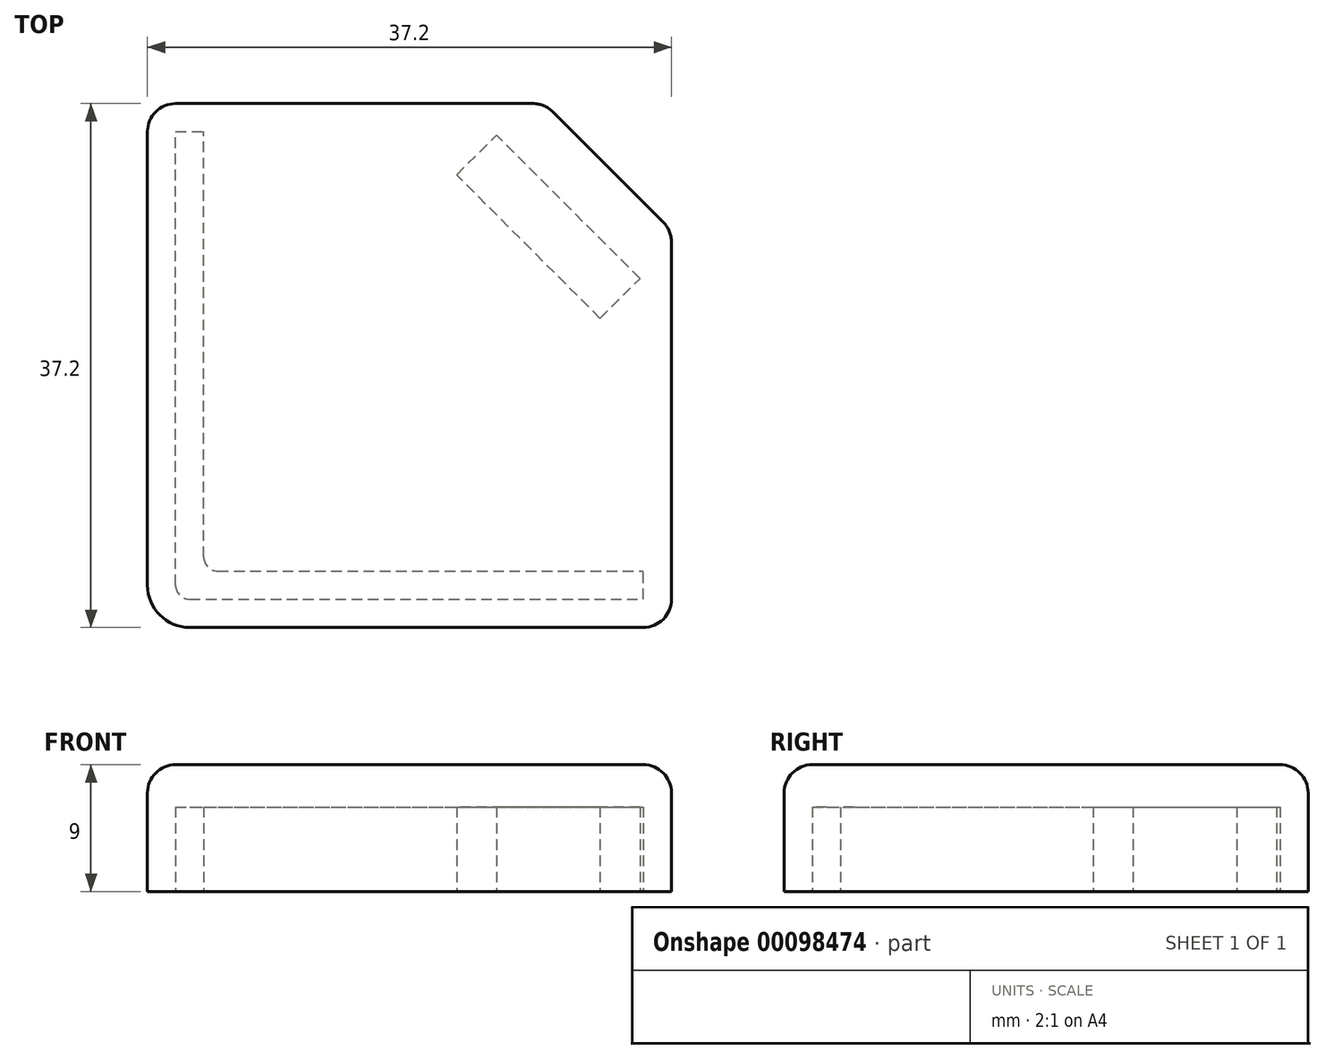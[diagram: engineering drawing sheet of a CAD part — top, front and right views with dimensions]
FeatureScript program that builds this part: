
annotation { "Feature Type Name" : "Feature", "Feature Type Description" : "" }
export const myFeature = defineFeature(function(context is Context, id is Id, definition is map)
    precondition{}
    {
        {
            var Q0;
            Q0=qCreatedBy(makeId("Top.planeOp"),FACE);
            var sketch = newSketch(context, id + "F0", { "sketchPlane" : qUnion([Q0])});
            skLineSegment(sketch, "E0", {"start": v(0, 0) * mm, "end": v(0, 32.2) * mm, "construction": true});
            skLineSegment(sketch, "E1", {"start": v(0, 0) * mm, "end": v(32.2, 0) * mm, "construction": true});
            skLineSegment(sketch, "E2.0", {"start": v(1, 2) * mm, "end": v(1, 32.2) * mm});
            skLineSegment(sketch, "E2.1", {"start": v(2, 1) * mm, "end": v(32.2, 1) * mm});
            skLineSegment(sketch, "E3.0", {"start": v(-1, 0) * mm, "end": v(-1, 32.2) * mm});
            skLineSegment(sketch, "E3.1", {"start": v(0, -1) * mm, "end": v(32.2, -1) * mm});
            skLineSegment(sketch, "E4", {"start": v(-1, 32.2) * mm, "end": v(1, 32.2) * mm});
            skLineSegment(sketch, "E5", {"start": v(32.2, -1) * mm, "end": v(32.2, 1) * mm});
            skPoint(sketch, "E6.visualSharp", {"position": v(1, 1) * mm});
            skArc(sketch, "E6.filletArc", {"start": v(1, 2) * mm, "mid": v(1.3, 1.3) * mm, "end": v(2, 1) * mm});
            skPoint(sketch, "E7.visualSharp", {"position": v(-1, -1) * mm});
            skArc(sketch, "E7.filletArc", {"start": v(-1, 0) * mm, "mid": v(-0.7, -0.7) * mm, "end": v(0, -1) * mm});
            skLineSegment(sketch, "E8.0", {"start": v(-3, 0) * mm, "end": v(-3, 34.2) * mm});
            skArc(sketch, "E8.1", {"start": v(-3, 0) * mm, "mid": v(-2.12, -2.12) * mm, "end": v(0, -3) * mm});
            skLineSegment(sketch, "E8.2", {"start": v(3, 5) * mm, "end": v(3, 34.2) * mm});
            skLineSegment(sketch, "E8.3", {"start": v(5, 3) * mm, "end": v(34.2, 3) * mm});
            skLineSegment(sketch, "E8.4", {"start": v(34.2, -3) * mm, "end": v(34.2, 3) * mm});
            skLineSegment(sketch, "E8.5", {"start": v(-3, 34.2) * mm, "end": v(3, 34.2) * mm});
            skLineSegment(sketch, "E8.6", {"start": v(0, -3) * mm, "end": v(34.2, -3) * mm});
            skPoint(sketch, "E9.visualSharp", {"position": v(3, 3) * mm});
            skArc(sketch, "E9.filletArc", {"start": v(3, 5) * mm, "mid": v(3.59, 3.59) * mm, "end": v(5, 3) * mm});
            skSolve(sketch);
        }
        {
            var Q0;
            Q0=makeQuery(id+"F0.imprint","IMPRINT",FACE,{"disambiguationData":[TD([[makeQuery(id+"F0.imprint","IMPRINT",EDGE,{"derivedFrom":sQuery(id+"F0.wireOp",EDGE,"E2.0")}),-1.0]])]});
            extrude(context, id + "F1", {"entities" : qUnion([Q0]), "depth" : 6 * mm});
        }
        {
            var Q0;
            Q0=makeQuery(id+"F1.opExtrude","CAP_FACE",FACE,{"disambiguationData":[OSD([sQuery(id+"F0.wireOp",EDGE,"E2.0"),sQuery(id+"F0.wireOp",EDGE,"E2.1"),sQuery(id+"F0.wireOp",EDGE,"E3.0"),sQuery(id+"F0.wireOp",EDGE,"E3.1"),sQuery(id+"F0.wireOp",EDGE,"E4"),sQuery(id+"F0.wireOp",EDGE,"E5"),sQuery(id+"F0.wireOp",EDGE,"E6.filletArc"),sQuery(id+"F0.wireOp",EDGE,"E7.filletArc"),sQuery(id+"F0.wireOp",EDGE,"E8.0"),sQuery(id+"F0.wireOp",EDGE,"E8.1"),sQuery(id+"F0.wireOp",EDGE,"E8.2"),sQuery(id+"F0.wireOp",EDGE,"E8.3"),sQuery(id+"F0.wireOp",EDGE,"E8.4"),sQuery(id+"F0.wireOp",EDGE,"E8.5"),sQuery(id+"F0.wireOp",EDGE,"E8.6"),sQuery(id+"F0.wireOp",EDGE,"E9.filletArc")])],"isStart":false});
            var sketch = newSketch(context, id + "F2", { "sketchPlane" : qUnion([Q0])});
            skLineSegment(sketch, "E10.0", {"start": v(-3, 34.2) * mm, "end": v(3, 34.2) * mm});
            skLineSegment(sketch, "E10.1", {"start": v(-3, 0) * mm, "end": v(-3, 34.2) * mm});
            skArc(sketch, "E10.2", {"start": v(-3, 0) * mm, "mid": v(-2.12, -2.12) * mm, "end": v(0, -3) * mm});
            skLineSegment(sketch, "E10.3", {"start": v(0, -3) * mm, "end": v(34.2, -3) * mm});
            skLineSegment(sketch, "E10.4", {"start": v(34.2, -3) * mm, "end": v(34.2, 3) * mm});
            skLineSegment(sketch, "E10.5", {"start": v(5, 3) * mm, "end": v(34.2, 3) * mm});
            skArc(sketch, "E10.6", {"start": v(3, 5) * mm, "mid": v(3.59, 3.59) * mm, "end": v(5, 3) * mm});
            skLineSegment(sketch, "E10.7", {"start": v(3, 5) * mm, "end": v(3, 34.2) * mm});
            skSolve(sketch);
        }
        {
            var Q0;
            Q0=qSketchRegion(id+"F2",true);
            var Q1;
            Q1=makeQuery(id+"F2.imprint","IMPRINT",FACE,{"disambiguationData":[TD([[makeQuery(id+"F2.imprint","IMPRINT",EDGE,{"derivedFrom":sQuery(id+"F2.wireOp",EDGE,"E10.0")}),-1.0]])]});
            var Q2;
            Q2=makeQuery(id+"F2.imprint","IMPRINT",FACE,{"disambiguationData":[TD([[makeQuery(id+"F2.imprint","IMPRINT",EDGE,{"derivedFrom":makeQuery(id+"F1.opExtrude","CAP_EDGE",EDGE,{"disambiguationData":[OSD([sQuery(id+"F0.wireOp",EDGE,"E2.0")])],"isStart":false})}),1.0]])]});
            extrude(context, id + "F3", {"entities" : qUnion([Q0, Q1, Q2]), "operationType" : NewBodyOperationType.ADD, "depth" : 3 * mm});
        }
        {
            var Q0;
            Q0=makeQuery(id+"F1.opExtrude","CAP_FACE",FACE,{"disambiguationData":[OSD([sQuery(id+"F0.wireOp",EDGE,"E2.0"),sQuery(id+"F0.wireOp",EDGE,"E2.1"),sQuery(id+"F0.wireOp",EDGE,"E3.0"),sQuery(id+"F0.wireOp",EDGE,"E3.1"),sQuery(id+"F0.wireOp",EDGE,"E4"),sQuery(id+"F0.wireOp",EDGE,"E5"),sQuery(id+"F0.wireOp",EDGE,"E6.filletArc"),sQuery(id+"F0.wireOp",EDGE,"E7.filletArc"),sQuery(id+"F0.wireOp",EDGE,"E8.0"),sQuery(id+"F0.wireOp",EDGE,"E8.1"),sQuery(id+"F0.wireOp",EDGE,"E8.2"),sQuery(id+"F0.wireOp",EDGE,"E8.3"),sQuery(id+"F0.wireOp",EDGE,"E8.4"),sQuery(id+"F0.wireOp",EDGE,"E8.5"),sQuery(id+"F0.wireOp",EDGE,"E8.6"),sQuery(id+"F0.wireOp",EDGE,"E9.filletArc")])],"isStart":true});
            var sketch = newSketch(context, id + "F4", { "sketchPlane" : qUnion([Q0])});
            skLineSegment(sketch, "E11", {"start": v(0, 0) * mm, "end": v(34.09, -34.09) * mm, "construction": true});
            skLineSegment(sketch, "E12", {"start": v(24.04, -24.04) * mm, "end": v(18.95, -29.13) * mm});
            skLineSegment(sketch, "E13", {"start": v(18.95, -29.13) * mm, "end": v(21.78, -31.96) * mm});
            skLineSegment(sketch, "E14", {"start": v(21.78, -31.96) * mm, "end": v(26.87, -26.87) * mm});
            skLineSegment(sketch, "E15.MirrorCS", {"start": v(31.96, -21.78) * mm, "end": v(26.87, -26.87) * mm});
            skLineSegment(sketch, "E16.MirrorCS", {"start": v(24.04, -24.04) * mm, "end": v(29.13, -18.95) * mm});
            skLineSegment(sketch, "E17.MirrorCS", {"start": v(29.13, -18.95) * mm, "end": v(31.96, -21.78) * mm});
            skLineSegment(sketch, "E18", {"start": v(3, -34.2) * mm, "end": v(25.2, -34.2) * mm});
            skLineSegment(sketch, "E19", {"start": v(34.2, -25.2) * mm, "end": v(34.2, -3) * mm});
            skLineSegment(sketch, "E20.0", {"start": v(5, -3) * mm, "end": v(34.2, -3) * mm});
            skArc(sketch, "E20.1", {"start": v(3, -5) * mm, "mid": v(3.59, -3.59) * mm, "end": v(5, -3) * mm});
            skLineSegment(sketch, "E20.2", {"start": v(3, -5) * mm, "end": v(3, -34.2) * mm});
            skLineSegment(sketch, "E21", {"start": v(29.7, -29.7) * mm, "end": v(34.2, -25.2) * mm});
            skLineSegment(sketch, "E22.MirrorCS", {"start": v(29.7, -29.7) * mm, "end": v(25.2, -34.2) * mm});
            skSolve(sketch);
        }
        {
            var Q0;
            Q0 = qSketchRegion(id + "F4", true);
            var Q1;
            Q1=makeQuery(id+"F3.opExtrude","CAP_FACE",FACE,{"disambiguationData":[OSD([sQuery(id+"F2.wireOp",EDGE,"E10.0"),sQuery(id+"F2.wireOp",EDGE,"E10.1"),sQuery(id+"F2.wireOp",EDGE,"E10.2"),sQuery(id+"F2.wireOp",EDGE,"E10.3"),sQuery(id+"F2.wireOp",EDGE,"E10.4"),sQuery(id+"F2.wireOp",EDGE,"E10.5"),sQuery(id+"F2.wireOp",EDGE,"E10.6"),sQuery(id+"F2.wireOp",EDGE,"E10.7")])],"isStart":false});
            extrude(context, id + "F5", {"entities" : qUnion([Q0]), "operationType" : NewBodyOperationType.ADD, "endBound" : BoundingType.UP_TO_SURFACE, "oppositeDirection" : true, "endBoundEntityFace" : qUnion([Q1]), "depth" : 25 * mm});
        }
        {
            var Q0;
            {var subQ0=sQuery(id+"F2.wireOp",EDGE,"E10.7");var subQ1=sQuery(id+"F2.wireOp",EDGE,"E10.6");var subQ2=sQuery(id+"F2.wireOp",EDGE,"E10.5");var subQ3=sQuery(id+"F2.wireOp",EDGE,"E10.4");var subQ4=sQuery(id+"F2.wireOp",EDGE,"E10.3");var subQ5=sQuery(id+"F2.wireOp",EDGE,"E10.2");var subQ6=sQuery(id+"F2.wireOp",EDGE,"E10.1");var subQ7=sQuery(id+"F2.wireOp",EDGE,"E10.0");Q0=makeQuery(id+"F5.boolean.opBoolean","MERGE",FACE,{"derivedFrom":[makeQuery(id+"F3.opExtrude","CAP_FACE",FACE,{"disambiguationData":[OSD([subQ7,subQ6,subQ5,subQ4,subQ3,subQ2,subQ1,subQ0])],"isStart":false}),makeQuery(id+"F5.opExtrude","CAP_FACE",FACE,{"disambiguationData":[OSD([subQ7,subQ6,subQ5,subQ4,subQ3,subQ2,subQ1,subQ0])],"isStart":false})]});}
            var sketch = newSketch(context, id + "F6", { "sketchPlane" : qUnion([Q0])});
            skLineSegment(sketch, "E23.0", {"start": v(29.13, 18.95) * mm, "end": v(18.95, 29.13) * mm});
            skLineSegment(sketch, "E23.1", {"start": v(29.13, 18.95) * mm, "end": v(31.96, 21.78) * mm});
            skLineSegment(sketch, "E23.2", {"start": v(31.96, 21.78) * mm, "end": v(21.78, 31.96) * mm});
            skLineSegment(sketch, "E23.3", {"start": v(18.95, 29.13) * mm, "end": v(21.78, 31.96) * mm});
            skSolve(sketch);
        }
        {
            var Q0;
            Q0 = qSketchRegion(id + "F6", true);
            extrude(context, id + "F7", {"entities" : qUnion([Q0]), "operationType" : NewBodyOperationType.ADD, "oppositeDirection" : true, "depth" : 3 * mm});
        }
        {
            var Q0;
            Q0=makeQuery(id+"F3.boolean.opBoolean","MERGE",EDGE,{"derivedFrom":[makeQuery(id+"F1.opExtrude","SWEPT_EDGE",EDGE,{"disambiguationData":[OSD([sQuery(id+"F0.wireOp",EDGE,"E8.4"),sQuery(id+"F0.wireOp",EDGE,"E8.6")])]}),makeQuery(id+"F3.opExtrude","SWEPT_EDGE",EDGE,{"disambiguationData":[OSD([sQuery(id+"F2.wireOp",EDGE,"E10.3"),sQuery(id+"F2.wireOp",EDGE,"E10.4")])]})]});
            var Q1;
            Q1=makeQuery(id+"F5.opExtrude","SWEPT_EDGE",EDGE,{"disambiguationData":[OSD([sQuery(id+"F4.wireOp",EDGE,"E19"),sQuery(id+"F4.wireOp",EDGE,"E21")])]});
            var Q2;
            Q2=makeQuery(id+"F5.opExtrude","SWEPT_EDGE",EDGE,{"disambiguationData":[OSD([sQuery(id+"F4.wireOp",EDGE,"E18"),sQuery(id+"F4.wireOp",EDGE,"E22.MirrorCS")])]});
            var Q3;
            Q3=makeQuery(id+"F3.boolean.opBoolean","MERGE",EDGE,{"derivedFrom":[makeQuery(id+"F1.opExtrude","SWEPT_EDGE",EDGE,{"disambiguationData":[OSD([sQuery(id+"F0.wireOp",EDGE,"E8.0"),sQuery(id+"F0.wireOp",EDGE,"E8.5")])]}),makeQuery(id+"F3.opExtrude","SWEPT_EDGE",EDGE,{"disambiguationData":[OSD([sQuery(id+"F2.wireOp",EDGE,"E10.0"),sQuery(id+"F2.wireOp",EDGE,"E10.1")])]})]});
            fillet(context, id + "F8", {"entities" : qUnion([Q0, Q1, Q2, Q3]), "radius" : 2 * mm, "tangentPropagation" : true, "allowEdgeOverflow" : false});
        }
        {
            var Q0;
            {var subQ0=sQuery(id+"F2.wireOp",EDGE,"E10.7");var subQ1=sQuery(id+"F2.wireOp",EDGE,"E10.6");var subQ2=sQuery(id+"F2.wireOp",EDGE,"E10.5");var subQ3=sQuery(id+"F2.wireOp",EDGE,"E10.4");var subQ4=sQuery(id+"F2.wireOp",EDGE,"E10.3");var subQ5=sQuery(id+"F2.wireOp",EDGE,"E10.2");var subQ6=sQuery(id+"F2.wireOp",EDGE,"E10.1");var subQ7=sQuery(id+"F2.wireOp",EDGE,"E10.0");Q0=makeQuery(id+"F7.boolean.opBoolean","MERGE",FACE,{"derivedFrom":[makeQuery(id+"F5.boolean.opBoolean","MERGE",FACE,{"derivedFrom":[makeQuery(id+"F3.opExtrude","CAP_FACE",FACE,{"disambiguationData":[OSD([subQ7,subQ6,subQ5,subQ4,subQ3,subQ2,subQ1,subQ0])],"isStart":false}),makeQuery(id+"F5.opExtrude","CAP_FACE",FACE,{"disambiguationData":[OSD([subQ7,subQ6,subQ5,subQ4,subQ3,subQ2,subQ1,subQ0])],"isStart":false})]}),makeQuery(id+"F7.opExtrude","CAP_FACE",FACE,{"disambiguationData":[OSD([sQuery(id+"F6.wireOp",EDGE,"E23.0"),sQuery(id+"F6.wireOp",EDGE,"E23.1"),sQuery(id+"F6.wireOp",EDGE,"E23.2"),sQuery(id+"F6.wireOp",EDGE,"E23.3")])],"isStart":true})]});}
            fillet(context, id + "F9", {"entities" : qUnion([Q0]), "radius" : 2 * mm, "tangentPropagation" : true, "allowEdgeOverflow" : false});
        }
    });
